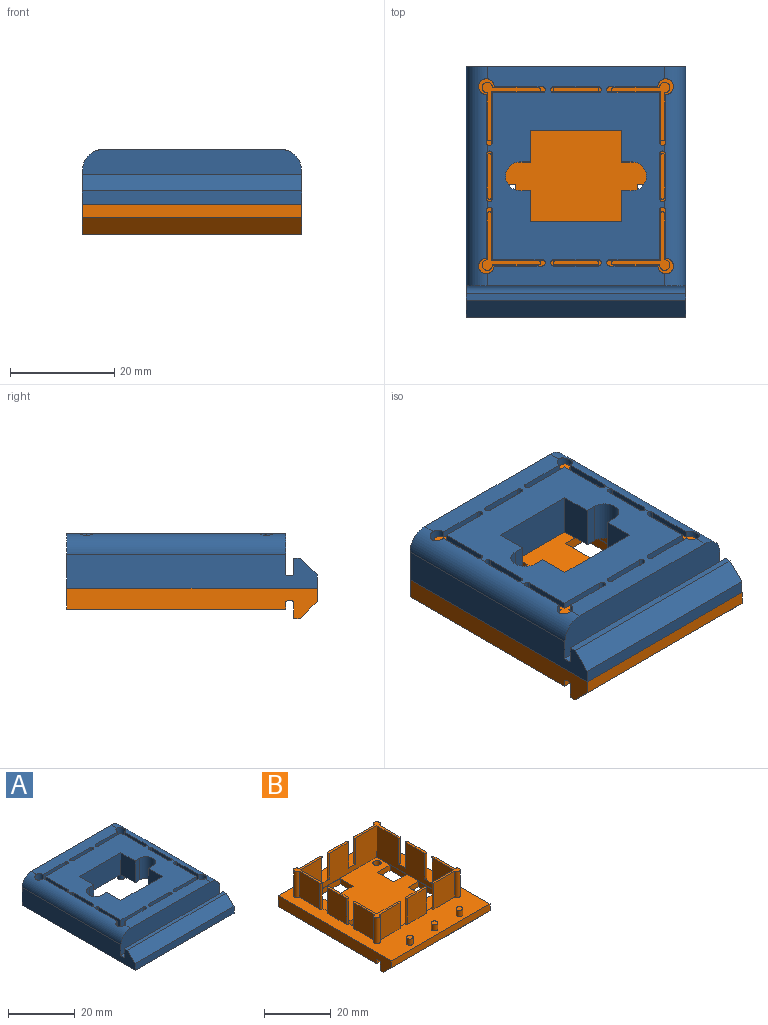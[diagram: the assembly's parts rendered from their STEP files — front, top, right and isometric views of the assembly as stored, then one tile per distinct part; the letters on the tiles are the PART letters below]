
ASSEMBLY  parts=2 mates=1
PART A: 98 faces, bbox 42x48x14.5 mm
  f0: plane 9.5x8mm, normal (0,1,0), area 76mm2, adj f10,f25,f60,f73
  f1: plane 8.5x8mm, normal (0,1,0), area 68mm2, adj f30,f31,f60,f73
  f2: plane 9.5x8mm, normal (1,0,0), area 76mm2, adj f26,f32,f60,f73
  f3: plane 8.5x8mm, normal (1,0,0), area 68mm2, adj f12,f13,f60,f73
  f4: plane 9.5x8mm, normal (1,0,0), area 76mm2, adj f5,f42,f60,f73
  f5: plane 9.5x8mm, normal (0,-1,0), area 76mm2, adj f4,f41,f60,f73
  f6: plane 8.5x8mm, normal (0,-1,0), area 68mm2, adj f45,f46,f60,f73
  f7: plane 9.5x8mm, normal (0,-1,0), area 76mm2, adj f8,f36,f60,f73
  f8: plane 9.5x8mm, normal (-1,0,0), area 76mm2, adj f7,f40,f60,f73
  f9: plane 8.5x8mm, normal (-1,0,0), area 68mm2, adj f47,f57,f60,f73
  f10: plane 9.5x8mm, normal (-1,0,0), area 76mm2, adj f0,f27,f60,f73
  f11: plane 42x7.95mm, normal (0,-1,0), area 327mm2, adj f50,f58,f60,f61,f62,f66
  f12: cylinder r=0.6mm len=8mm, axis (0,0,-1), area 15.1mm2, adj f3,f59,f60,f61,f73
  f13: cylinder r=0.6mm len=8mm, axis (0,0,-1), area 15.1mm2, adj f3,f59,f60,f61,f73
  f14: plane 8x6mm, normal (1,0,0), area 48mm2, adj f15,f51,f60,f73
  f15: plane 17.5x8mm, normal (0,-1,0), area 140mm2, adj f14,f16,f60,f73
  f16: plane 8x6mm, normal (-1,0,0), area 48mm2, adj f15,f17,f60,f73
  f17: plane 8x2mm, normal (0,-1,0), area 16mm2, adj f16,f18,f60,f73
  f18: cylinder r=2.75mm len=8mm, axis (0,0,-1), area 69.1mm2, adj f17,f19,f60,f73
  f19: plane 8x2mm, normal (0,1,0), area 16mm2, adj f18,f20,f60,f73
  f20: plane 8x6mm, normal (-1,0,0), area 48mm2, adj f19,f21,f60,f73
  f21: plane 17.5x8mm, normal (0,1,0), area 140mm2, adj f20,f22,f60,f73
  f22: plane 8x6mm, normal (1,0,0), area 48mm2, adj f21,f23,f60,f73
  f23: plane 8x2mm, normal (0,1,0), area 16mm2, adj f22,f24,f60,f73
  f24: cylinder r=2.75mm len=8mm, axis (0,0,-1), area 69.1mm2, adj f23,f51,f60,f73
  f25: cylinder r=0.6mm len=8mm, axis (0,0,-1), area 15.1mm2, adj f0,f52,f60,f73
  f26: plane 9.5x8mm, normal (0,1,0), area 76mm2, adj f2,f33,f60,f73
  f27: cylinder r=0.6mm len=8mm, axis (0,0,-1), area 15.1mm2, adj f10,f28,f60,f62,f73
  f28: plane 9.2x8mm, normal (1,0,0), area 73.6mm2, adj f27,f29,f62,f73
  f29: cylinder r=1.5mm len=8mm, axis (0,0,-1), area 55.6mm2, adj f28,f52,f60,f62,f73
  f30: cylinder r=0.6mm len=8mm, axis (0,0,-1), area 15.1mm2, adj f1,f53,f60,f73
  f31: cylinder r=0.6mm len=8mm, axis (0,0,-1), area 15.1mm2, adj f1,f53,f60,f73
  f32: cylinder r=0.6mm len=8mm, axis (0,0,-1), area 15.1mm2, adj f2,f54,f60,f61,f73
  f33: cylinder r=0.6mm len=8mm, axis (0,0,-1), area 15.1mm2, adj f26,f34,f60,f73
  f34: plane 9.2x8mm, normal (0,-1,0), area 73.6mm2, adj f33,f35,f60,f73
  f35: cylinder r=1.5mm len=8mm, axis (0,0,-1), area 55.6mm2, adj f34,f54,f60,f61,f73
  f36: cylinder r=0.6mm len=8mm, axis (0,0,-1), area 15.1mm2, adj f7,f37,f60,f73
  f37: plane 9.2x8mm, normal (0,1,0), area 73.6mm2, adj f36,f38,f60,f73
  f38: cylinder r=1.5mm len=8mm, axis (0,0,-1), area 55.6mm2, adj f37,f39,f60,f62,f73
  f39: plane 9.2x8mm, normal (1,0,0), area 73.6mm2, adj f38,f40,f62,f73
  f40: cylinder r=0.6mm len=8mm, axis (0,0,-1), area 15.1mm2, adj f8,f39,f60,f62,f73
  f41: cylinder r=0.6mm len=8mm, axis (0,0,-1), area 15.1mm2, adj f5,f55,f60,f73
  f42: cylinder r=0.6mm len=8mm, axis (0,0,-1), area 15.1mm2, adj f4,f43,f60,f61,f73
  f43: plane 9.2x8mm, normal (-1,0,0), area 73.6mm2, adj f42,f44,f61,f73
  f44: cylinder r=1.5mm len=8mm, axis (0,0,-1), area 55.6mm2, adj f43,f55,f60,f61,f73
  f45: cylinder r=0.6mm len=8mm, axis (0,0,-1), area 15.1mm2, adj f6,f56,f60,f73
  f46: cylinder r=0.6mm len=8mm, axis (0,0,-1), area 15.1mm2, adj f6,f56,f60,f73
  f47: cylinder r=0.6mm len=8mm, axis (0,0,-1), area 15.1mm2, adj f9,f48,f60,f62,f73
  f48: plane 8.5x8mm, normal (1,0,0), area 68mm2, adj f47,f57,f62,f73
  f49: plane 42x10.5mm, normal (0,1,0), area 434.1mm2, adj f50,f58,f60,f61,f62,f65
  f50: plane 48x6.5mm, normal (-1,0,0), area 297.4mm2, adj f11,f49,f62,f63,f64,f65,f66,f67
  f51: plane 8x2mm, normal (0,-1,0), area 16mm2, adj f14,f24,f60,f73
  f52: plane 9.2x8mm, normal (0,-1,0), area 73.6mm2, adj f25,f29,f60,f73
  f53: plane 8.5x8mm, normal (0,-1,0), area 68mm2, adj f30,f31,f60,f73
  f54: plane 9.2x8mm, normal (-1,0,0), area 73.6mm2, adj f32,f35,f61,f73
  f55: plane 9.2x8mm, normal (0,1,0), area 73.6mm2, adj f41,f44,f60,f73
  f56: plane 8.5x8mm, normal (0,1,0), area 68mm2, adj f45,f46,f60,f73
  f57: cylinder r=0.6mm len=8mm, axis (0,0,-1), area 15.1mm2, adj f9,f48,f60,f62,f73
  f58: plane 48x6.5mm, normal (1,0,0), area 297.4mm2, adj f11,f49,f61,f63,f64,f65,f66,f67
  f59: plane 8.5x8mm, normal (-1,0,0), area 68mm2, adj f12,f13,f61,f73
  f60: plane 42x34mm, normal (0,0,1), area 935.8mm2, adj f0,f1,f2,f3,f4,f5,f6,f7
  f61: cylinder r=4mm len=42mm, axis (0,-1,0), area 249.8mm2, adj f11,f12,f13,f32,f35,f42,f43,f44
  f62: cylinder r=4mm len=42mm, axis (0,1,0), area 249.8mm2, adj f11,f27,f28,f29,f38,f39,f40,f47
  f63: plane 42x3.25mm, normal (0,-0.71,0.71), area 193mm2, adj f50,f58,f64,f68
  f64: plane 42x2.55mm, normal (0,-1,0), area 107.1mm2, adj f50,f58,f63,f65
  f65: plane 48x42mm, normal (0,0,-1), area 480.3mm2, adj f49,f50,f58,f64,f69,f70,f71,f72
  f66: cylinder r=1.5mm len=42mm, axis (-1,0,0), area 66mm2, adj f11,f50,f58,f67
  f67: plane 42x3.25mm, normal (0,1,0), area 136.5mm2, adj f50,f58,f66,f68
  f68: plane 42x1.25mm, normal (0,0,1), area 52.5mm2, adj f50,f58,f63,f67
  f69: plane 39x2.5mm, normal (1,0,0), area 97.5mm2, adj f65,f70,f72,f73
  f70: plane 39x2.5mm, normal (0,-1,0), area 97.5mm2, adj f65,f69,f71,f73
  f71: plane 39x2.5mm, normal (-1,0,0), area 97.5mm2, adj f65,f70,f72,f73
  f72: plane 39x2.5mm, normal (0,1,0), area 97.5mm2, adj f65,f69,f71,f73
  f73: plane 39x39mm, normal (0,0,-1), area 938mm2, adj f0,f1,f2,f3,f4,f5,f6,f7
  f74: cylinder r=1.25mm len=2.5mm, axis (0,0,-1), area 19.6mm2, adj f65,f75
  f75: plane 2.5x2.5mm, normal (0,0,-1), area 4.9mm2, adj f74
  f76: cylinder r=1.25mm len=2.5mm, axis (0,0,-1), area 19.6mm2, adj f65,f77
  f77: plane 2.5x2.5mm, normal (0,0,-1), area 4.9mm2, adj f76
  f78: cylinder r=1.25mm len=2.5mm, axis (0,0,-1), area 19.6mm2, adj f65,f79
  f79: plane 2.5x2.5mm, normal (0,0,-1), area 4.9mm2, adj f78
  f80: plane 9.75x3.25mm, normal (0,0,-1), area 31.7mm2, adj f81,f82,f83,f84
  f81: plane 9.75x4mm, normal (0,1,0), area 39mm2, adj f73,f80,f82,f84
  f82: plane 4x3.25mm, normal (1,0,0), area 13mm2, adj f73,f80,f81,f83
  f83: plane 9.75x4mm, normal (0,-1,0), area 39mm2, adj f73,f80,f82,f84
  f84: plane 4x3.25mm, normal (-1,0,0), area 13mm2, adj f73,f80,f81,f83
  f85: plane 1.95x1.95mm, normal (0,0,-1), area 3mm2, adj f86
  f86: cylinder r=0.97mm len=6.5mm, axis (0,0,1), area 39.8mm2, adj f73,f85
  f87: plane 1.95x1.95mm, normal (0,0,-1), area 3mm2, adj f88
  f88: cylinder r=0.97mm len=6.5mm, axis (0,0,1), area 39.8mm2, adj f73,f87
  f89: plane 1.95x1.95mm, normal (0,0,-1), area 3mm2, adj f90
  f90: cylinder r=0.97mm len=6.5mm, axis (0,0,1), area 39.8mm2, adj f73,f89
  f91: plane 1.95x1.95mm, normal (0,0,-1), area 3mm2, adj f92
  f92: cylinder r=0.97mm len=6.5mm, axis (0,0,1), area 39.8mm2, adj f73,f91
  f93: plane 5.94x3.25mm, normal (0,0,-1), area 19.3mm2, adj f94,f95,f96,f97
  f94: plane 4x3.25mm, normal (0,-1,0), area 13mm2, adj f73,f93,f95,f97
  f95: plane 5.94x4mm, normal (-1,0,0), area 23.7mm2, adj f73,f93,f94,f96
  f96: plane 4x3.25mm, normal (0,1,0), area 13mm2, adj f73,f93,f95,f97
  f97: plane 5.94x4mm, normal (1,0,0), area 23.7mm2, adj f73,f93,f94,f96
PART B: 82 faces, bbox 42x48x15.3 mm
  f0: plane 48x42mm, normal (0,0,1), area 857.6mm2, adj f21,f23,f24,f29,f31,f32,f33,f34
  f1: plane 5.5x2mm, normal (1,0,0), area 11mm2, adj f2,f20,f25,f81
  f2: plane 11x2mm, normal (0,-1,0), area 22mm2, adj f1,f3,f25,f81
  f3: plane 5.5x2mm, normal (-1,0,0), area 11mm2, adj f2,f20,f25,f81
  f4: plane 7x2mm, normal (-1,0,0), area 14mm2, adj f5,f13,f25,f81
  f5: plane 5.5x2mm, normal (0,1,0), area 11mm2, adj f4,f6,f25,f81
  f6: plane 7x2mm, normal (1,0,0), area 14mm2, adj f5,f13,f25,f81
  f7: plane 4.4x2mm, normal (0,-1,0), area 8.8mm2, adj f8,f18,f25,f81
  f8: plane 8x2mm, normal (-1,0,0), area 16mm2, adj f7,f9,f25,f81
  f9: plane 4.4x2mm, normal (0,1,0), area 8.8mm2, adj f8,f18,f25,f81
  f10: plane 4.5x2mm, normal (0,1,0), area 9mm2, adj f11,f19,f25,f81
  f11: plane 8x2mm, normal (1,0,0), area 16mm2, adj f10,f12,f25,f81
  f12: plane 4.5x2mm, normal (0,-1,0), area 9mm2, adj f11,f19,f25,f81
  f13: plane 5.5x2mm, normal (0,-1,0), area 11mm2, adj f4,f6,f25,f81
  f14: cylinder r=1.25mm len=2.5mm, axis (0,0,1), area 15.7mm2, adj f25,f81
  f15: cylinder r=1.25mm len=2.5mm, axis (0,0,1), area 15.7mm2, adj f25,f81
  f16: cylinder r=1.25mm len=2.5mm, axis (0,0,1), area 15.7mm2, adj f25,f81
  f17: cylinder r=1.25mm len=2.5mm, axis (0,0,1), area 15.7mm2, adj f25,f81
  f18: plane 8x2mm, normal (1,0,0), area 16mm2, adj f7,f9,f25,f81
  f19: plane 8x2mm, normal (-1,0,0), area 16mm2, adj f10,f12,f25,f81
  f20: plane 11x2mm, normal (0,1,0), area 22mm2, adj f1,f3,f25,f81
  f21: plane 48x5.8mm, normal (-1,0,0), area 192.4mm2, adj f0,f22,f24,f25,f26,f27,f28,f29
  f22: plane 42x1.45mm, normal (0,-1,0), area 60.9mm2, adj f21,f23,f25,f28
  f23: plane 48x5.8mm, normal (1,0,0), area 192.4mm2, adj f0,f22,f24,f25,f26,f27,f28,f29
  f24: plane 42x4mm, normal (0,1,0), area 168mm2, adj f0,f21,f23,f25
  f25: plane 42x42mm, normal (0,0,-1), area 1574.2mm2, adj f1,f2,f3,f4,f5,f6,f7,f8
  f26: plane 42x1.25mm, normal (0,0,-1), area 52.5mm2, adj f21,f23,f27,f30
  f27: plane 42x3.25mm, normal (0,1,0), area 136.5mm2, adj f21,f23,f26,f28
  f28: cylinder r=1.5mm len=42mm, axis (-1,0,0), area 66mm2, adj f21,f22,f23,f27
  f29: plane 42x2.55mm, normal (0,-1,0), area 107.1mm2, adj f0,f21,f23,f30
  f30: plane 42x3.25mm, normal (0,-0.71,-0.71), area 193mm2, adj f21,f23,f26,f29
  f31: cylinder r=0.4mm len=9.5mm, axis (0,0,-1), area 11.9mm2, adj f0,f32,f34,f35
  f32: plane 32.4x11.5mm, normal (-1,0,0), area 311.8mm2, adj f0,f31,f33,f35,f36,f46,f61,f62
  f33: cylinder r=0.4mm len=9.5mm, axis (0,0,-1), area 11.9mm2, adj f0,f32,f34,f35
  f34: plane 9.5x8mm, normal (1,0,0), area 76mm2, adj f0,f31,f33,f35
  f35: plane 8.8x0.8mm, normal (0,0,1), area 6.9mm2, adj f31,f32,f33,f34
  f36: plane 32.4x11.5mm, normal (0,-1,0), area 311.8mm2, adj f0,f32,f37,f39,f40,f41,f54,f56
  f37: cylinder r=0.4mm len=9.5mm, axis (0,0,-1), area 11.9mm2, adj f0,f36,f38,f40
  f38: plane 9.5x8mm, normal (0,1,0), area 76mm2, adj f0,f37,f39,f40
  f39: cylinder r=0.4mm len=9.5mm, axis (0,0,-1), area 11.9mm2, adj f0,f36,f38,f40
  f40: plane 8.8x0.8mm, normal (0,0,1), area 6.9mm2, adj f36,f37,f38,f39
  f41: plane 32.4x11.5mm, normal (1,0,0), area 311.8mm2, adj f0,f36,f42,f44,f45,f46,f53,f56
  f42: cylinder r=0.4mm len=9.5mm, axis (0,0,-1), area 11.9mm2, adj f0,f41,f43,f45
  f43: plane 9.5x8mm, normal (-1,0,0), area 76mm2, adj f0,f42,f44,f45
  f44: cylinder r=0.4mm len=9.5mm, axis (0,0,-1), area 11.9mm2, adj f0,f41,f43,f45
  f45: plane 8.8x0.8mm, normal (0,0,1), area 6.9mm2, adj f41,f42,f43,f44
  f46: plane 32.4x11.5mm, normal (0,1,0), area 311.8mm2, adj f0,f32,f41,f47,f49,f50,f65,f68
  f47: cylinder r=0.4mm len=9.5mm, axis (0,0,-1), area 11.9mm2, adj f0,f46,f48,f50
  f48: plane 9.5x8mm, normal (0,-1,0), area 76mm2, adj f0,f47,f49,f50
  f49: cylinder r=0.4mm len=9.5mm, axis (0,0,-1), area 11.9mm2, adj f0,f46,f48,f50
  f50: plane 8.8x0.8mm, normal (0,0,1), area 6.9mm2, adj f46,f47,f48,f49
  f51: cylinder r=1mm len=9.5mm, axis (0,0,-1), area 44.8mm2, adj f0,f52,f55,f56
  f52: plane 9.5x8.8mm, normal (-1,0,0), area 83.6mm2, adj f0,f51,f53,f56
  f53: cylinder r=0.4mm len=9.5mm, axis (0,0,-1), area 11.9mm2, adj f0,f41,f52,f56
  f54: cylinder r=0.4mm len=9.5mm, axis (0,0,-1), area 11.9mm2, adj f0,f36,f55,f56
  f55: plane 9.5x8.8mm, normal (0,1,0), area 83.6mm2, adj f0,f51,f54,f56
  f56: plane 11.2x11.2mm, normal (0,0,1), area 17.9mm2, adj f36,f41,f51,f52,f53,f54,f55
  f57: plane 9.5x8.8mm, normal (1,0,0), area 83.6mm2, adj f0,f58,f61,f62
  f58: cylinder r=1mm len=9.5mm, axis (0,0,-1), area 44.8mm2, adj f0,f57,f59,f62
  f59: plane 9.5x8.8mm, normal (0,1,0), area 83.6mm2, adj f0,f58,f60,f62
  f60: cylinder r=0.4mm len=9.5mm, axis (0,0,-1), area 11.9mm2, adj f0,f36,f59,f62
  f61: cylinder r=0.4mm len=9.5mm, axis (0,0,-1), area 11.9mm2, adj f0,f32,f57,f62
  f62: plane 11.2x11.2mm, normal (0,0,1), area 17.9mm2, adj f32,f36,f57,f58,f59,f60,f61
  f63: cylinder r=1mm len=9.5mm, axis (0,0,-1), area 44.8mm2, adj f0,f64,f67,f68
  f64: plane 9.5x8.8mm, normal (0,-1,0), area 83.6mm2, adj f0,f63,f65,f68
  f65: cylinder r=0.4mm len=9.5mm, axis (0,0,-1), area 11.9mm2, adj f0,f46,f64,f68
  f66: cylinder r=0.4mm len=9.5mm, axis (0,0,-1), area 11.9mm2, adj f0,f41,f67,f68
  f67: plane 9.5x8.8mm, normal (-1,0,0), area 83.6mm2, adj f0,f63,f66,f68
  f68: plane 11.2x11.2mm, normal (0,0,1), area 17.9mm2, adj f41,f46,f63,f64,f65,f66,f67
  f69: cylinder r=1mm len=9.5mm, axis (0,0,-1), area 44.8mm2, adj f0,f70,f73,f74
  f70: plane 9.5x8.8mm, normal (1,0,0), area 83.6mm2, adj f0,f69,f71,f74
  f71: cylinder r=0.4mm len=9.5mm, axis (0,0,-1), area 11.9mm2, adj f0,f32,f70,f74
  f72: cylinder r=0.4mm len=9.5mm, axis (0,0,-1), area 11.9mm2, adj f0,f46,f73,f74
  f73: plane 9.5x8.8mm, normal (0,-1,0), area 83.6mm2, adj f0,f69,f72,f74
  f74: plane 11.2x11.2mm, normal (0,0,1), area 17.9mm2, adj f32,f46,f69,f70,f71,f72,f73
  f75: cylinder r=1mm len=2.25mm, axis (0,0,-1), area 14.1mm2, adj f0,f76
  f76: plane 2x2mm, normal (0,0,1), area 3.1mm2, adj f75
  f77: cylinder r=1mm len=2.25mm, axis (0,0,-1), area 14.1mm2, adj f0,f78
  f78: plane 2x2mm, normal (0,0,1), area 3.1mm2, adj f77
  f79: cylinder r=1mm len=2.25mm, axis (0,0,-1), area 14.1mm2, adj f0,f80
  f80: plane 2x2mm, normal (0,0,1), area 3.1mm2, adj f79
  f81: plane 32.4x32.4mm, normal (0,0,1), area 859.9mm2, adj f1,f2,f3,f4,f5,f6,f7,f8
PLACE A t=(0.04,20.29,29.53)mm
PLACE B t=(0.04,20.29,28.03)mm
MATE slider B.f77 <-> A.f76  axis (0,0,-1) through (0.04,-4.21,28.03)mm
